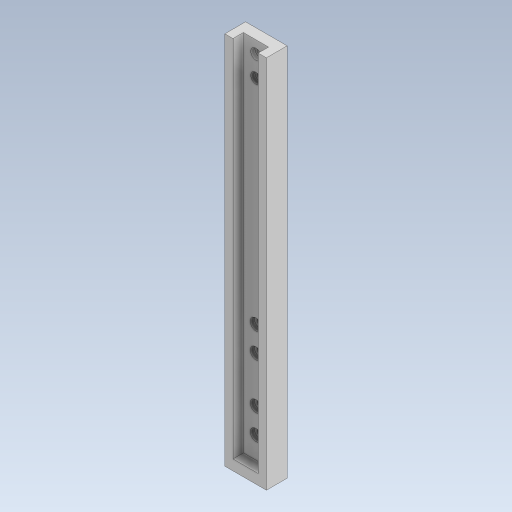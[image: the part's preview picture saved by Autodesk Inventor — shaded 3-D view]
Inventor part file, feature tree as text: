
AUTODESK INVENTOR PART (.ipt)
format: ipt  version: 2023.5 (Build 275446000, 446)  size: 309,760 bytes
history: native  units: in
note: dims shown in document units (in); Inventor stores cm internally (conversion verified against a paired STEP export)
features: extrude x7, sketch x5
ambient origin geometry x8: Origin, YZ Plane, XZ Plane, XY Plane, X Axis, Y Axis, Z Axis, Center Point
bodies: Solid1 (feature_tree)
feature tree (12):
  extrude  "Extrusion1"  Depth=0.3937in
  extrude  "Extrusion2"  Depth=0.4764in
  sketch  "Sketch3"  dims[d5=5.7087in d6=0.0in d7=0.1181in]
  extrude  "Extrusion3"  Depth=0.1181in
  extrude  "Extrusion4"  Depth=0.4134in
  extrude  "Extrusion5"  Depth=0.0787in
  sketch  "Sketch6"  dims[d10=0.1181in d11=0.4724in d12=0.2165in d13=0.2165in d14=0.1969in d15=0.0in d16=0.0787in d17=0.0in d18=1.1811in d19=0.0in d24=0.1181in d25=0.1181in d26=0.2362in d27=0.3937in d28=0.1969in d29=0.1969in d30=0.1969in d31=0.0in d32=0.0787in d33=0.0in d34=0.4331in]
  extrude  "Extrusion6"  Depth=0.0787in
  extrude  "Extrusion7"  Depth=0.0787in
  sketch  "Sketch1"  dims[d0=5.9055in d1=0.3937in]
  sketch  "Sketch2"  dims[d2=0.7874in d3=0.0in d4=0.4764in]
  sketch  "Sketch4"  dims[d8=0.2382in d9=0.4134in]
